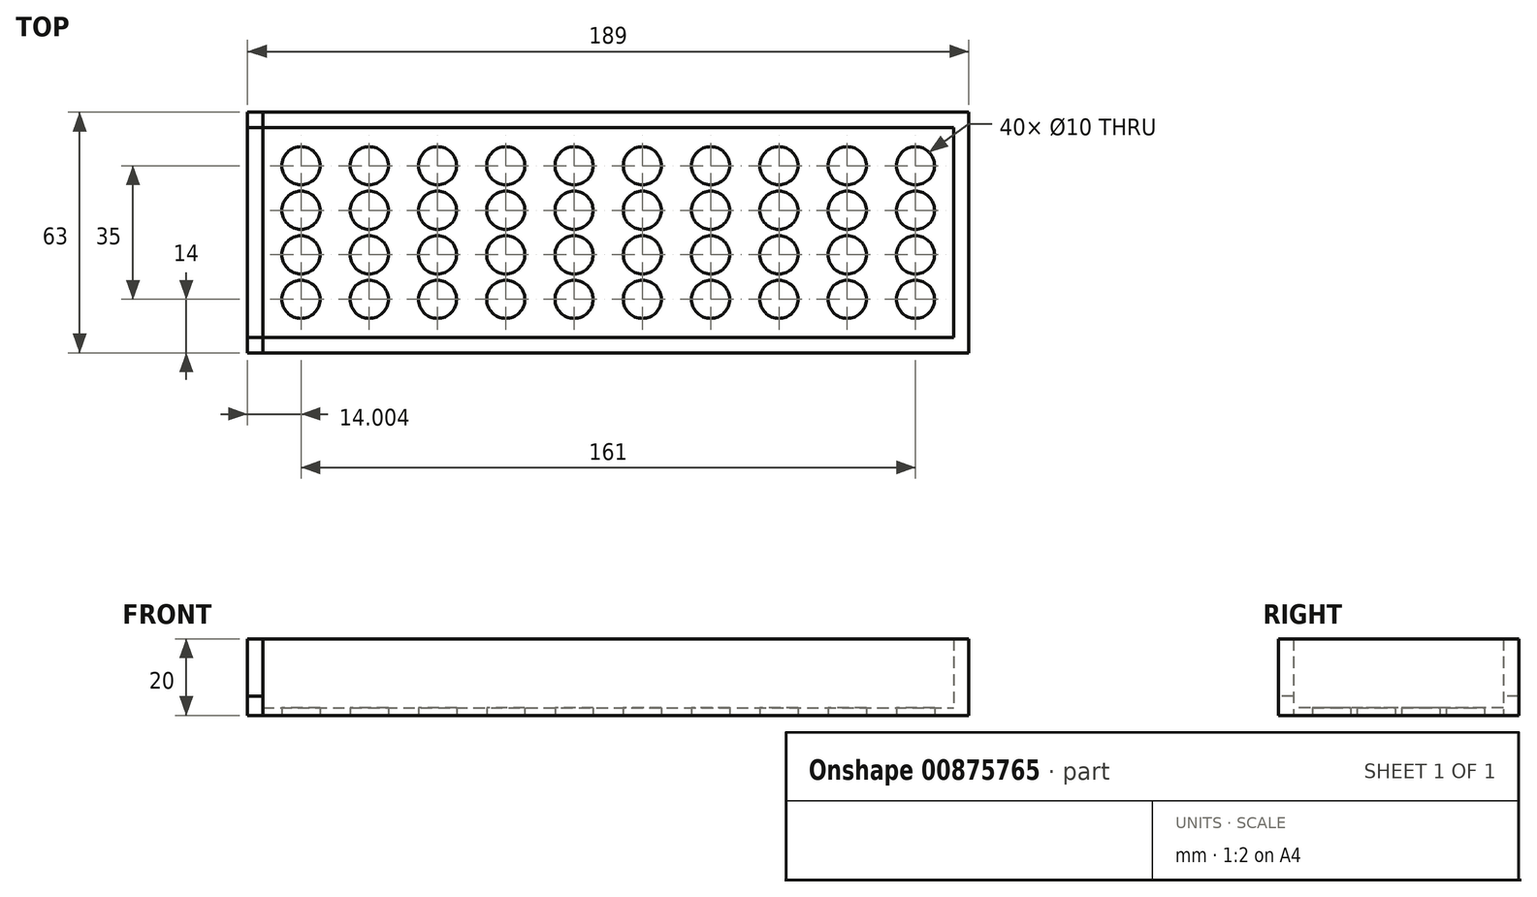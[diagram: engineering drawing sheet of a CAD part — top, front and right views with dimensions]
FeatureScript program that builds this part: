
annotation { "Feature Type Name" : "Feature", "Feature Type Description" : "" }
export const myFeature = defineFeature(function(context is Context, id is Id, definition is map)
    precondition{}
    {
        {
            var Q0;
            Q0=qCreatedBy(makeId("Top.planeOp"),FACE);
            var sketch = newSketch(context, id + "F0", { "sketchPlane" : qUnion([Q0])});
            skLineSegment(sketch, "E0.bottom", {"start": v(-84.7, 27.5) * mm, "end": v(96.3, 27.5) * mm});
            skLineSegment(sketch, "E0.top", {"start": v(-84.7, -27.5) * mm, "end": v(96.3, -27.5) * mm});
            skLineSegment(sketch, "E0.left", {"start": v(-84.7, 27.5) * mm, "end": v(-84.7, -27.5) * mm});
            skLineSegment(sketch, "E0.right", {"start": v(96.3, 27.5) * mm, "end": v(96.3, -27.5) * mm});
            skPoint(sketch, "E0.middle", {"position": v(5.8, 0) * mm});
            skLineSegment(sketch, "E1.0", {"start": v(-88.7, 31.5) * mm, "end": v(100.3, 31.5) * mm});
            skLineSegment(sketch, "E1.1", {"start": v(-88.7, 31.5) * mm, "end": v(-88.7, -31.5) * mm});
            skLineSegment(sketch, "E1.2", {"start": v(-88.7, -31.5) * mm, "end": v(100.3, -31.5) * mm});
            skLineSegment(sketch, "E1.3", {"start": v(100.3, 31.5) * mm, "end": v(100.3, -31.5) * mm});
            skLineSegment(sketch, "E2", {"start": v(-84.7, 27.5) * mm, "end": v(-84.7, 31.5) * mm});
            skLineSegment(sketch, "E3", {"start": v(-84.7, 31.5) * mm, "end": v(-84.7, -31.5) * mm});
            skLineSegment(sketch, "E4", {"start": v(96.3, 27.5) * mm, "end": v(96.3, 31.5) * mm});
            skLineSegment(sketch, "E5", {"start": v(96.3, 31.5) * mm, "end": v(96.3, -31.5) * mm});
            skCircle(sketch, "E6", {"center": v(-74.7, 17.5) * mm, "radius": 5 * mm});
            skCircle(sketch, "E7.0.1.0", {"center": v(-74.7, 5.83) * mm, "radius": 5 * mm});
            skCircle(sketch, "E7.0.2.0", {"center": v(-74.7, -5.83) * mm, "radius": 5 * mm});
            skCircle(sketch, "E7.0.3.0", {"center": v(-74.7, -17.5) * mm, "radius": 5 * mm});
            skCircle(sketch, "E7.1.0.0", {"center": v(-56.8, 17.5) * mm, "radius": 5 * mm});
            skCircle(sketch, "E7.1.1.0", {"center": v(-56.8, 5.83) * mm, "radius": 5 * mm});
            skCircle(sketch, "E7.1.2.0", {"center": v(-56.8, -5.83) * mm, "radius": 5 * mm});
            skCircle(sketch, "E7.1.3.0", {"center": v(-56.8, -17.5) * mm, "radius": 5 * mm});
            skCircle(sketch, "E7.2.0.0", {"center": v(-38.92, 17.5) * mm, "radius": 5 * mm});
            skCircle(sketch, "E7.2.1.0", {"center": v(-38.92, 5.83) * mm, "radius": 5 * mm});
            skCircle(sketch, "E7.2.2.0", {"center": v(-38.92, -5.83) * mm, "radius": 5 * mm});
            skCircle(sketch, "E7.2.3.0", {"center": v(-38.92, -17.5) * mm, "radius": 5 * mm});
            skCircle(sketch, "E7.3.0.0", {"center": v(-21.03, 17.5) * mm, "radius": 5 * mm});
            skCircle(sketch, "E7.3.1.0", {"center": v(-21.03, 5.83) * mm, "radius": 5 * mm});
            skCircle(sketch, "E7.3.2.0", {"center": v(-21.03, -5.83) * mm, "radius": 5 * mm});
            skCircle(sketch, "E7.3.3.0", {"center": v(-21.03, -17.5) * mm, "radius": 5 * mm});
            skCircle(sketch, "E7.4.0.0", {"center": v(-3.14, 17.5) * mm, "radius": 5 * mm});
            skCircle(sketch, "E7.4.1.0", {"center": v(-3.14, 5.83) * mm, "radius": 5 * mm});
            skCircle(sketch, "E7.4.2.0", {"center": v(-3.14, -5.83) * mm, "radius": 5 * mm});
            skCircle(sketch, "E7.4.3.0", {"center": v(-3.14, -17.5) * mm, "radius": 5 * mm});
            skCircle(sketch, "E7.5.0.0", {"center": v(14.75, 17.5) * mm, "radius": 5 * mm});
            skCircle(sketch, "E7.5.1.0", {"center": v(14.75, 5.83) * mm, "radius": 5 * mm});
            skCircle(sketch, "E7.5.2.0", {"center": v(14.75, -5.83) * mm, "radius": 5 * mm});
            skCircle(sketch, "E7.5.3.0", {"center": v(14.75, -17.5) * mm, "radius": 5 * mm});
            skCircle(sketch, "E7.6.0.0", {"center": v(32.64, 17.5) * mm, "radius": 5 * mm});
            skCircle(sketch, "E7.6.1.0", {"center": v(32.64, 5.83) * mm, "radius": 5 * mm});
            skCircle(sketch, "E7.6.2.0", {"center": v(32.64, -5.83) * mm, "radius": 5 * mm});
            skCircle(sketch, "E7.6.3.0", {"center": v(32.64, -17.5) * mm, "radius": 5 * mm});
            skCircle(sketch, "E7.7.0.0", {"center": v(50.53, 17.5) * mm, "radius": 5 * mm});
            skCircle(sketch, "E7.7.1.0", {"center": v(50.53, 5.83) * mm, "radius": 5 * mm});
            skCircle(sketch, "E7.7.2.0", {"center": v(50.53, -5.83) * mm, "radius": 5 * mm});
            skCircle(sketch, "E7.7.3.0", {"center": v(50.53, -17.5) * mm, "radius": 5 * mm});
            skCircle(sketch, "E7.8.0.0", {"center": v(68.42, 17.5) * mm, "radius": 5 * mm});
            skCircle(sketch, "E7.8.1.0", {"center": v(68.42, 5.83) * mm, "radius": 5 * mm});
            skCircle(sketch, "E7.8.2.0", {"center": v(68.42, -5.83) * mm, "radius": 5 * mm});
            skCircle(sketch, "E7.8.3.0", {"center": v(68.42, -17.5) * mm, "radius": 5 * mm});
            skCircle(sketch, "E7.9.0.0", {"center": v(86.3, 17.5) * mm, "radius": 5 * mm});
            skCircle(sketch, "E7.9.1.0", {"center": v(86.3, 5.83) * mm, "radius": 5 * mm});
            skCircle(sketch, "E7.9.2.0", {"center": v(86.3, -5.83) * mm, "radius": 5 * mm});
            skCircle(sketch, "E7.9.3.0", {"center": v(86.3, -17.5) * mm, "radius": 5 * mm});
            skLineSegment(sketch, "E7.direction1", {"start": v(-74.7, 17.5) * mm, "end": v(-56.8, 17.5) * mm, "construction": true});
            skLineSegment(sketch, "E7.direction2", {"start": v(-74.7, 17.5) * mm, "end": v(-74.7, 5.83) * mm, "construction": true});
            skLineSegment(sketch, "E8", {"start": v(96.3, 27.5) * mm, "end": v(100.3, 27.5) * mm});
            skLineSegment(sketch, "E9", {"start": v(96.3, -27.5) * mm, "end": v(100.3, -27.5) * mm});
            skLineSegment(sketch, "E10", {"start": v(-84.7, -27.5) * mm, "end": v(-88.7, -27.5) * mm});
            skLineSegment(sketch, "E11", {"start": v(-84.7, 27.5) * mm, "end": v(-88.7, 27.5) * mm});
            skSolve(sketch);
        }
        {
            var Q0;
            {var subQ0=sQuery(id+"F0.wireOp",EDGE,"E10");Q0=makeQuery(id+"F0.imprint","IMPRINT",FACE,{"disambiguationData":[TD([[makeQuery(id+"F0.imprint","IMPRINT",EDGE,{"derivedFrom":subQ0}),-1.0]])]});}
            var Q1;
            {var subQ0=sQuery(id+"F0.wireOp",EDGE,"E0.top");Q1=makeQuery(id+"F0.imprint","IMPRINT",FACE,{"disambiguationData":[TD([[makeQuery(id+"F0.imprint","IMPRINT",EDGE,{"derivedFrom":subQ0}),-1.0]])]});}
            var Q2;
            {var subQ0=sQuery(id+"F0.wireOp",EDGE,"E0.bottom");Q2=makeQuery(id+"F0.imprint","IMPRINT",FACE,{"disambiguationData":[TD([[makeQuery(id+"F0.imprint","IMPRINT",EDGE,{"derivedFrom":subQ0}),1.0]])]});}
            var Q3;
            {var subQ0=sQuery(id+"F0.wireOp",EDGE,"E8");Q3=makeQuery(id+"F0.imprint","IMPRINT",FACE,{"disambiguationData":[TD([[makeQuery(id+"F0.imprint","IMPRINT",EDGE,{"derivedFrom":subQ0}),-1.0]])]});}
            extrude(context, id + "F1", {"entities" : qUnion([Q0, Q1, Q2, Q3]), "depth" : 20 * mm, "offsetDistance" : 25 * mm});
        }
        {
            var Q0;
            {var subQ5=sQuery(id+"F0.wireOp",EDGE,"E8");Q0=makeQuery(id+"F0.imprint","IMPRINT",FACE,{"disambiguationData":[TD([[makeQuery(id+"F0.imprint","IMPRINT",EDGE,{"derivedFrom":subQ5}),1.0]])]});}
            var Q1;
            {var subQ5=sQuery(id+"F0.wireOp",EDGE,"E9");Q1=makeQuery(id+"F0.imprint","IMPRINT",FACE,{"disambiguationData":[TD([[makeQuery(id+"F0.imprint","IMPRINT",EDGE,{"derivedFrom":subQ5}),-1.0]])]});}
            var Q2;
            {var subQ3=sQuery(id+"F0.wireOp",EDGE,"E10");Q2=makeQuery(id+"F0.imprint","IMPRINT",FACE,{"disambiguationData":[TD([[makeQuery(id+"F0.imprint","IMPRINT",EDGE,{"derivedFrom":subQ3}),1.0]])]});}
            var Q3;
            {var subQ5=sQuery(id+"F0.wireOp",EDGE,"E11");Q3=makeQuery(id+"F0.imprint","IMPRINT",FACE,{"disambiguationData":[TD([[makeQuery(id+"F0.imprint","IMPRINT",EDGE,{"derivedFrom":subQ5}),-1.0]])]});}
            extrude(context, id + "F2", {"entities" : qUnion([Q0, Q1, Q2, Q3]), "depth" : 20 * mm, "offsetDistance" : 25 * mm, "hasSecondDirection" : true, "secondDirectionOppositeDirection" : false, "secondDirectionDepth" : 5 * mm});
        }
        {
            var Q0;
            {var subQ1=sQuery(id+"F0.wireOp",EDGE,"E0.bottom");Q0=makeQuery(id+"F0.imprint","IMPRINT",FACE,{"disambiguationData":[TD([[makeQuery(id+"F0.imprint","IMPRINT",EDGE,{"derivedFrom":subQ1}),-1.0]])]});}
            extrude(context, id + "F3", {"entities" : qUnion([Q0]), "depth" : 2 * mm, "offsetDistance" : 25 * mm});
        }
        {
            var Q0;
            {var subQ0=sQuery(id+"F0.wireOp",EDGE,"E8");Q0=makeQuery(id+"F0.imprint","IMPRINT",FACE,{"disambiguationData":[TD([[makeQuery(id+"F0.imprint","IMPRINT",EDGE,{"derivedFrom":subQ0}),-1.0]])]});}
            extrude(context, id + "F4", {"entities" : qUnion([Q0]), "depth" : 15 * mm, "offsetDistance" : 25 * mm});
        }
        {
            var Q0;
            {var subQ5=sQuery(id+"F0.wireOp",EDGE,"E8");Q0=makeQuery(id+"F0.imprint","IMPRINT",FACE,{"disambiguationData":[TD([[makeQuery(id+"F0.imprint","IMPRINT",EDGE,{"derivedFrom":subQ5}),1.0]])]});}
            var Q1;
            {var subQ5=sQuery(id+"F0.wireOp",EDGE,"E9");Q1=makeQuery(id+"F0.imprint","IMPRINT",FACE,{"disambiguationData":[TD([[makeQuery(id+"F0.imprint","IMPRINT",EDGE,{"derivedFrom":subQ5}),-1.0]])]});}
            extrude(context, id + "F5", {"entities" : qUnion([Q0, Q1]), "operationType" : NewBodyOperationType.ADD, "depth" : 20 * mm, "offsetDistance" : 25 * mm});
        }
    });
